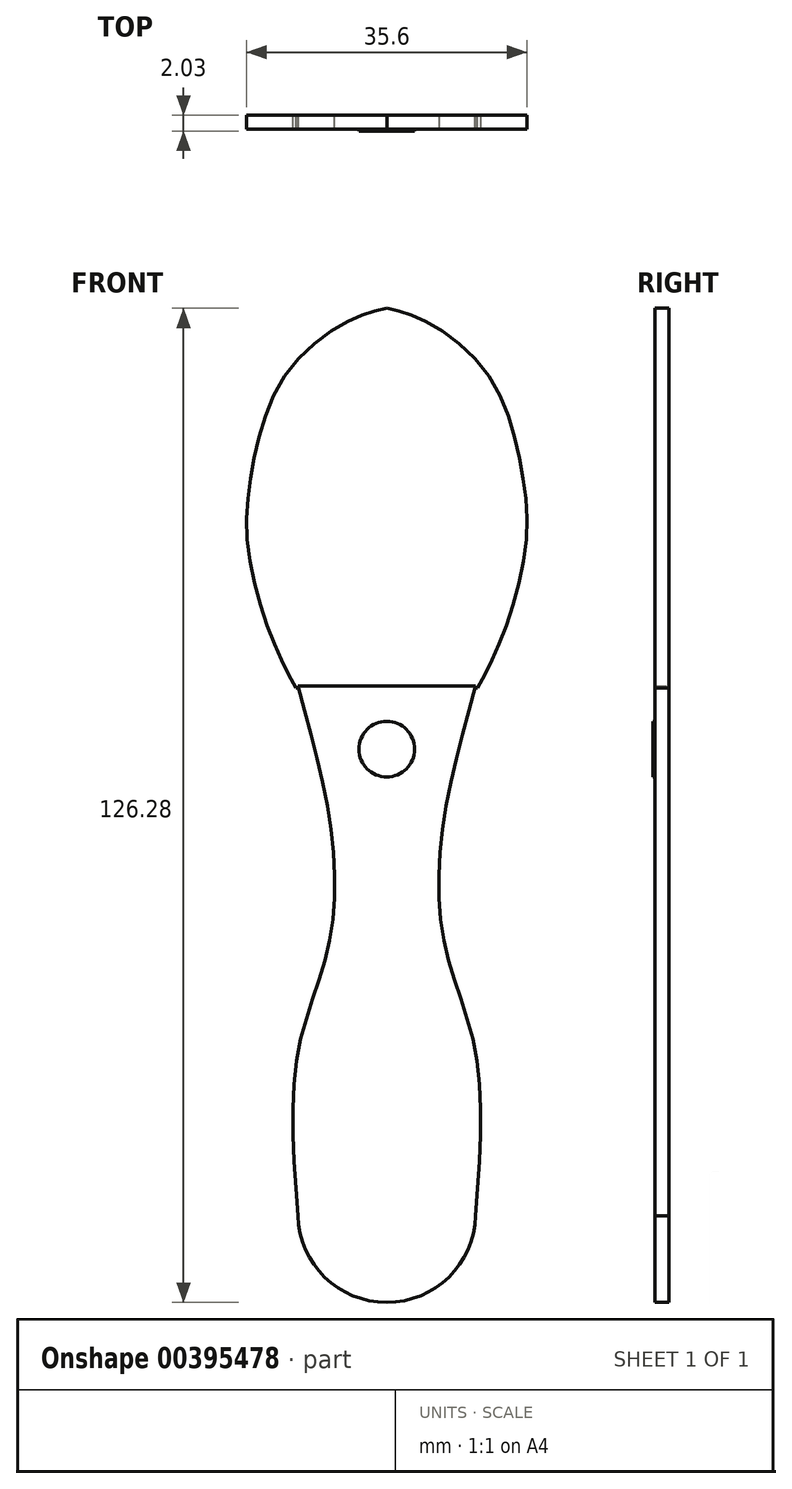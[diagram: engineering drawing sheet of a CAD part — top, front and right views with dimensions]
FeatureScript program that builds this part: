
annotation { "Feature Type Name" : "Feature", "Feature Type Description" : "" }
export const myFeature = defineFeature(function(context is Context, id is Id, definition is map)
    precondition{}
    {
        {
            var Q0;
            Q0=qCreatedBy(makeId("Front.planeOp"),FACE);
            var sketch = newSketch(context, id + "F0", { "sketchPlane" : qUnion([Q0])});
            skLineSegment(sketch, "E0.top", {"start": v(0, 18.36) * mm, "end": v(-11.3, 18.36) * mm});
            skPoint(sketch, "E0.middle", {"position": v(0, -15.3) * mm});
            skFitSpline(sketch, "E1", {"points": [v(-11.3, 18.36) * mm, v(-7.06, 0) * mm, v(-7.53, -15.3) * mm, v(-11.3, -28.24) * mm, v(-11.3, -48.95) * mm], "startDerivative": vector(19.72, -70.37) * mm, "endDerivative": vector(5.77, -80.31) * mm});
            skPoint(sketch, "E2.1.internal.orphan", {"position": v(0, -52.95) * mm});
            skArc(sketch, "E3", {"start": v(-11.3, -48.95) * mm, "mid": v(-7.88, -56.73) * mm, "end": v(0, -59.92) * mm});
            skPoint(sketch, "E4.endSnap0", {"position": v(0, -59.92) * mm});
            skPoint(sketch, "E5.1.internal.orphan", {"position": v(9.18, 12.18) * mm});
            skPoint(sketch, "E5.2.internal.orphan", {"position": v(7.06, 0) * mm});
            skPoint(sketch, "E5.3.internal.orphan", {"position": v(7.53, -15.3) * mm});
            skPoint(sketch, "E5.4.internal.orphan", {"position": v(11.3, -28.24) * mm});
            skPoint(sketch, "E5.5.internal.orphan", {"position": v(11.3, -41.55) * mm});
            skPoint(sketch, "E5.6.internal.orphan", {"position": v(11.3, -48.95) * mm});
            skLineSegment(sketch, "E6.trimOffspring", {"start": v(0, -48.62) * mm, "end": v(0, -52.95) * mm});
            skPoint(sketch, "E4.start.orphan", {"position": v(0, 18.36) * mm});
            skPoint(sketch, "E7.trimOffspring.end.orphan", {"position": v(0, -64.48) * mm});
            skPoint(sketch, "E8.orphan", {"position": v(11.3, 18.36) * mm});
            skLineSegment(sketch, "E9", {"start": v(0, 18.36) * mm, "end": v(0, -59.92) * mm, "construction": true});
            skFitSpline(sketch, "E10.MirrorCS", {"points": [v(11.3, 18.36) * mm, v(7.06, 0) * mm, v(7.53, -15.3) * mm, v(11.3, -28.24) * mm, v(11.3, -48.95) * mm], "startDerivative": vector(-19.72, -70.37) * mm, "endDerivative": vector(-5.77, -80.31) * mm});
            skArc(sketch, "E11.MirrorCS", {"start": v(11.3, -48.95) * mm, "mid": v(7.88, -56.73) * mm, "end": v(0, -59.92) * mm});
            skLineSegment(sketch, "E12.MirrorCS", {"start": v(0, 18.36) * mm, "end": v(11.3, 18.36) * mm});
            skSolve(sketch);
        }
        {
            var Q0;
            Q0=makeQuery(id+"F0.imprint","IMPRINT",FACE,{"disambiguationData":[TD([[makeQuery(id+"F0.imprint","IMPRINT",EDGE,{"derivedFrom":sQuery(id+"F0.wireOp",EDGE,"E0.top")}),1.0]])]});
            var sketch = newSketch(context, id + "F1", { "sketchPlane" : qUnion([Q0])});
            skFitSpline(sketch, "E13", {"points": [v(-11.53, 18.12) * mm, v(-14.6, 24.47) * mm, v(-17.65, 36.24) * mm, v(-16.94, 46.83) * mm, v(-12.7, 58.12) * mm, v(-4.47, 64.95) * mm, v(0, 66.36) * mm], "startDerivative": vector(-21.35, 39.32) * mm, "endDerivative": vector(34.81, 7.4) * mm});
            skLineSegment(sketch, "E14", {"start": v(0, 66.36) * mm, "end": v(0, 18.36) * mm, "construction": true});
            skFitSpline(sketch, "E15.MirrorCS", {"points": [v(11.53, 18.12) * mm, v(14.6, 24.47) * mm, v(17.65, 36.24) * mm, v(16.94, 46.83) * mm, v(12.7, 58.12) * mm, v(4.47, 64.95) * mm, v(0, 66.36) * mm], "startDerivative": vector(21.35, 39.32) * mm, "endDerivative": vector(-34.81, 7.4) * mm});
            skLineSegment(sketch, "E16", {"start": v(-11.53, 18.12) * mm, "end": v(11.53, 18.12) * mm});
            skSolve(sketch);
        }
        {
            var Q0;
            {var subQ4=sQuery(id+"F1.wireOp",EDGE,"E13");Q0=makeQuery(id+"F1.imprint","IMPRINT",FACE,{"disambiguationData":[TD([[makeQuery(id+"F1.imprint","IMPRINT",EDGE,{"derivedFrom":subQ4}),-1.0]])]});}
            var Q1;
            Q1=makeQuery(id+"F0.imprint","IMPRINT",FACE,{"disambiguationData":[TD([[makeQuery(id+"F0.imprint","IMPRINT",EDGE,{"derivedFrom":sQuery(id+"F0.wireOp",EDGE,"E0.top")}),1.0]])]});
            extrude(context, id + "F2", {"entities" : qUnion([Q0, Q1]), "depth" : 1.78 * mm});
        }
        {
            var Q0;
            Q0=makeQuery(id+"F2.opExtrude","CAP_FACE",FACE,{"disambiguationData":[OSD([sQuery(id+"F0.wireOp",EDGE,"E0.top"),sQuery(id+"F0.wireOp",EDGE,"E1"),sQuery(id+"F0.wireOp",EDGE,"E3"),sQuery(id+"F0.wireOp",EDGE,"E10.MirrorCS"),sQuery(id+"F0.wireOp",EDGE,"E11.MirrorCS"),sQuery(id+"F0.wireOp",EDGE,"E12.MirrorCS")])],"isStart":false});
            var sketch = newSketch(context, id + "F3", { "sketchPlane" : qUnion([Q0])});
            skCircle(sketch, "E17", {"center": v(0, 10.35) * mm, "radius": 3.54 * mm});
            skSolve(sketch);
        }
        {
            var Q0;
            Q0=makeQuery(id+"F3.imprint","IMPRINT",FACE,{"disambiguationData":[TD([[makeQuery(id+"F3.imprint","IMPRINT",EDGE,{"derivedFrom":sQuery(id+"F3.wireOp",EDGE,"E17")}),1.0]])]});
            extrude(context, id + "F4", {"entities" : qUnion([Q0]), "operationType" : NewBodyOperationType.ADD, "depth" : 0.25 * mm});
        }
    });
